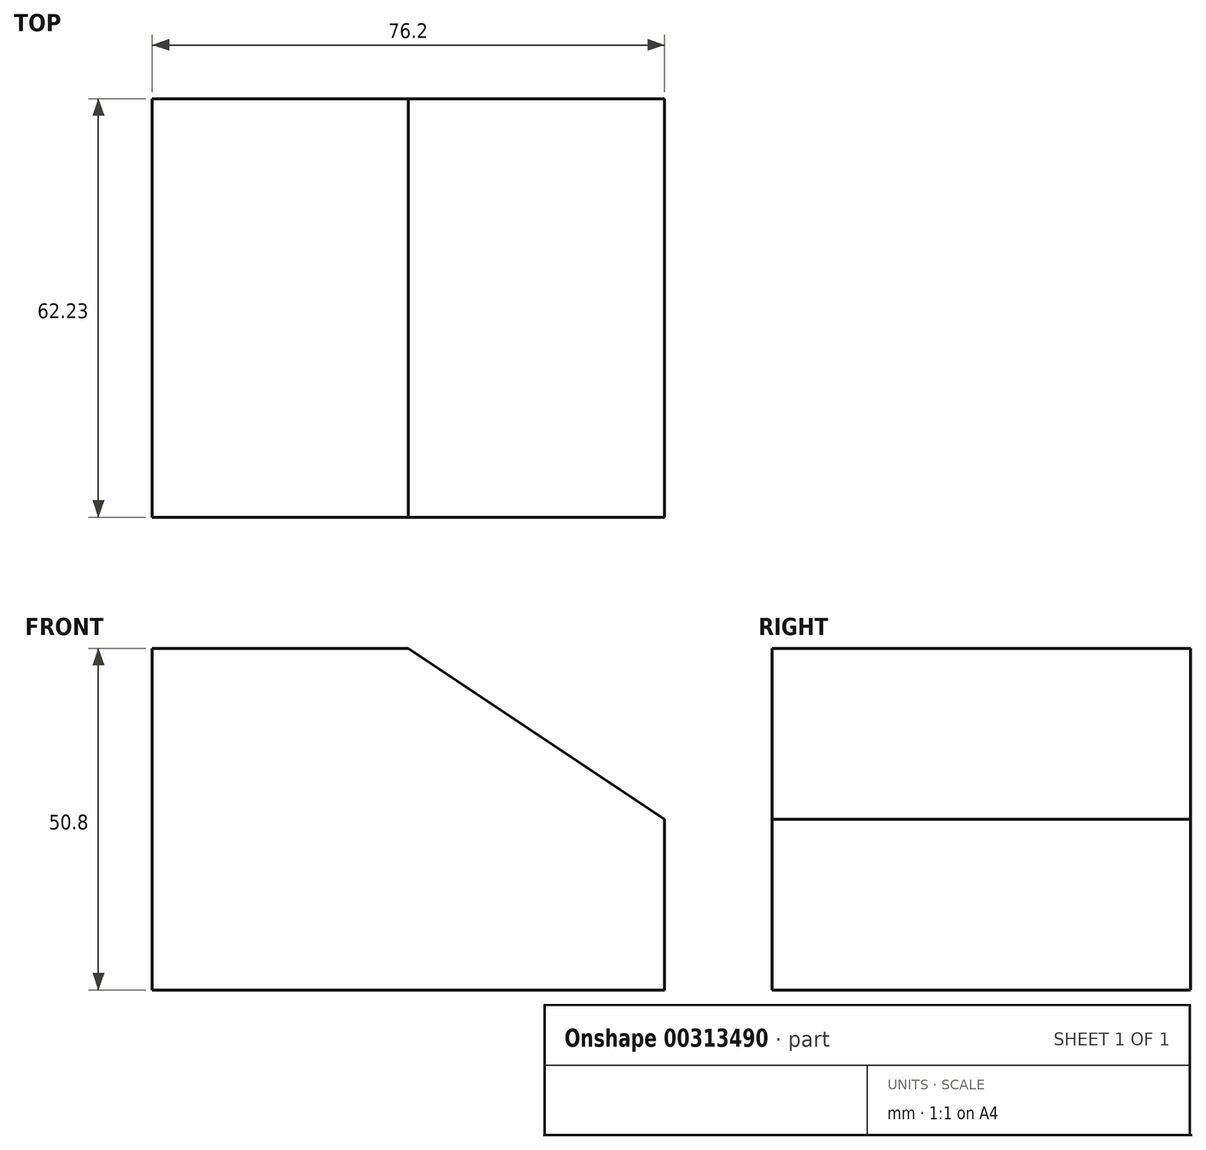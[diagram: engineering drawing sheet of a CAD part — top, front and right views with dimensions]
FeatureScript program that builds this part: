
annotation { "Feature Type Name" : "Feature", "Feature Type Description" : "" }
export const myFeature = defineFeature(function(context is Context, id is Id, definition is map)
    precondition{}
    {
        {
            var Q0;
            Q0=qCreatedBy(makeId("Front.planeOp"),FACE);
            var sketch = newSketch(context, id + "F0", { "sketchPlane" : qUnion([Q0])});
            skLineSegment(sketch, "E0", {"start": v(-38.1, -41.82) * mm, "end": v(38.1, -41.82) * mm});
            skLineSegment(sketch, "E1", {"start": v(38.1, -41.82) * mm, "end": v(38.1, -16.42) * mm});
            skLineSegment(sketch, "E2", {"start": v(-38.1, -41.82) * mm, "end": v(-38.1, 8.98) * mm});
            skLineSegment(sketch, "E3", {"start": v(-38.1, 8.98) * mm, "end": v(0, 8.98) * mm});
            skLineSegment(sketch, "E4", {"start": v(0, 8.98) * mm, "end": v(38.1, -16.42) * mm});
            skSolve(sketch);
        }
        {
            var Q0;
            Q0=makeQuery(id+"F0.imprint","IMPRINT",FACE,{"disambiguationData":[TD([[makeQuery(id+"F0.imprint","IMPRINT",EDGE,{"derivedFrom":sQuery(id+"F0.wireOp",EDGE,"E0")}),1.0]])]});
            extrude(context, id + "F1", {"entities" : qUnion([Q0]), "oppositeDirection" : true, "depth" : 62.23 * mm});
        }
    });
